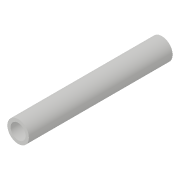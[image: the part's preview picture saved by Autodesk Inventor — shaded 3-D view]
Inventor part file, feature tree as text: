
AUTODESK INVENTOR PART (.ipt)
format: ipt  version: 2018 (Build 220112000, 112)  size: 76,800 bytes
history: native  units: in
note: dims shown in document units (in); Inventor stores cm internally (conversion verified against a paired STEP export)
features: extrude x1, sketch x1
ambient origin geometry x8: Origin, YZ Plane, XZ Plane, XY Plane, X Axis, Y Axis, Z Axis, Center Point
bodies: Solid1 (feature_tree)
feature tree (2):
  extrude  "Extrusion1"  Depth=1.5748in
  sketch  "Sketch1"  dims[d0=0.1654in d1=0.2362in d2=1.5748in d3=0.0in]
